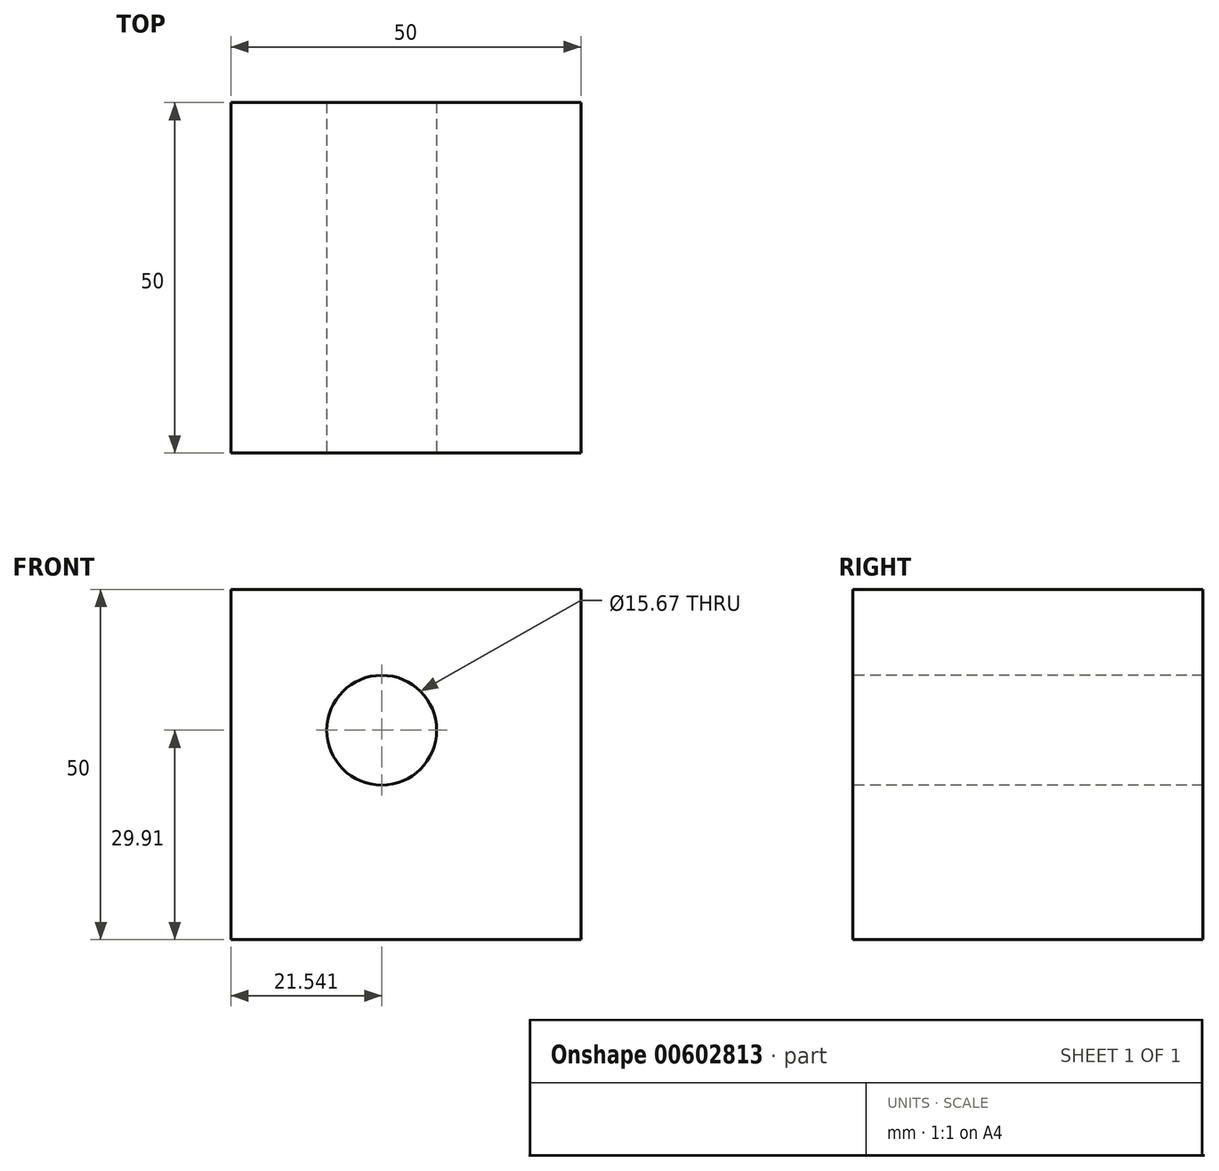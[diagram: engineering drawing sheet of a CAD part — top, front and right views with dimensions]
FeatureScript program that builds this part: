
annotation { "Feature Type Name" : "Feature", "Feature Type Description" : "" }
export const myFeature = defineFeature(function(context is Context, id is Id, definition is map)
    precondition{}
    {
        {
            var Q0;
            Q0=qCreatedBy(makeId("Front.planeOp"),FACE);
            var sketch = newSketch(context, id + "F0", { "sketchPlane" : qUnion([Q0])});
            skLineSegment(sketch, "E0.bottom", {"start": v(0, 0) * mm, "end": v(50, 0) * mm});
            skLineSegment(sketch, "E0.top", {"start": v(0, 50) * mm, "end": v(50, 50) * mm});
            skLineSegment(sketch, "E0.left", {"start": v(0, 0) * mm, "end": v(0, 50) * mm});
            skLineSegment(sketch, "E0.right", {"start": v(50, 0) * mm, "end": v(50, 50) * mm});
            skSolve(sketch);
        }
        {
            var Q0;
            Q0=makeQuery(id+"F0.imprint","IMPRINT",FACE,{"disambiguationData":[TD([[makeQuery(id+"F0.imprint","IMPRINT",EDGE,{"derivedFrom":sQuery(id+"F0.wireOp",EDGE,"E0.bottom")}),1.0]])]});
            extrude(context, id + "F1", {"entities" : qUnion([Q0]), "oppositeDirection" : true, "depth" : 50 * mm, "offsetDistance" : 25.4 * mm});
        }
        {
            var Q0;
            Q0=makeQuery(id+"F1.opExtrude","CAP_FACE",FACE,{"disambiguationData":[OSD([sQuery(id+"F0.wireOp",EDGE,"E0.bottom"),sQuery(id+"F0.wireOp",EDGE,"E0.top"),sQuery(id+"F0.wireOp",EDGE,"E0.left"),sQuery(id+"F0.wireOp",EDGE,"E0.right")])],"isStart":true});
            var sketch = newSketch(context, id + "F2", { "sketchPlane" : qUnion([Q0])});
            skCircle(sketch, "E1", {"center": v(21.54, 29.91) * mm, "radius": 7.84 * mm});
            skSolve(sketch);
        }
        {
            var Q0;
            Q0=makeQuery(id+"F2.imprint","IMPRINT",FACE,{"disambiguationData":[TD([[makeQuery(id+"F2.imprint","IMPRINT",EDGE,{"derivedFrom":sQuery(id+"F2.wireOp",EDGE,"E1")}),1.0]])]});
            extrude(context, id + "F3", {"entities" : qUnion([Q0]), "operationType" : NewBodyOperationType.REMOVE, "oppositeDirection" : true, "depth" : 60 * mm, "offsetDistance" : 25.4 * mm});
        }
    });
